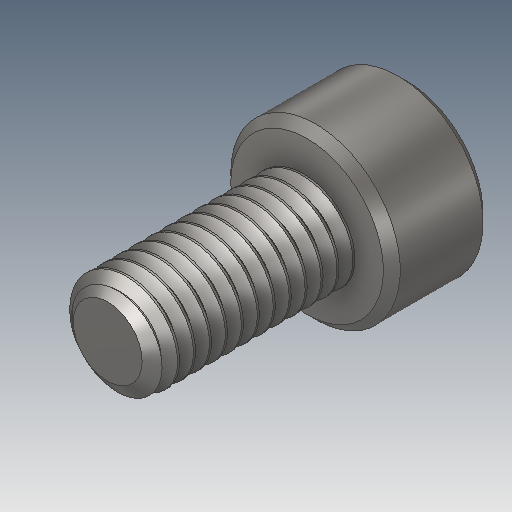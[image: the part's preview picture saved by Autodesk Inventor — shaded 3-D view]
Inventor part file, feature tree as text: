
AUTODESK INVENTOR PART (.ipt)
format: ipt  version: 2017 (Build 210142000, 142)  size: 538,624 bytes
history: native  units: in
note: dims shown in document units (in); Inventor stores cm internally (conversion verified against a paired STEP export)
features: chamfer x1
ambient origin geometry x8: Origin, YZ Plane, XZ Plane, XY Plane, X Axis, Y Axis, Z Axis, Center Point
bodies: Solid1 (feature_tree)
feature tree (1):
  chamfer  "Chamfer1"  [1 undecoded]
note: 1 required parameter value undecoded (feature->parameter linkage not recoverable at this tier; creation-order binding heuristic only, values carry confidence <= 0.55)
